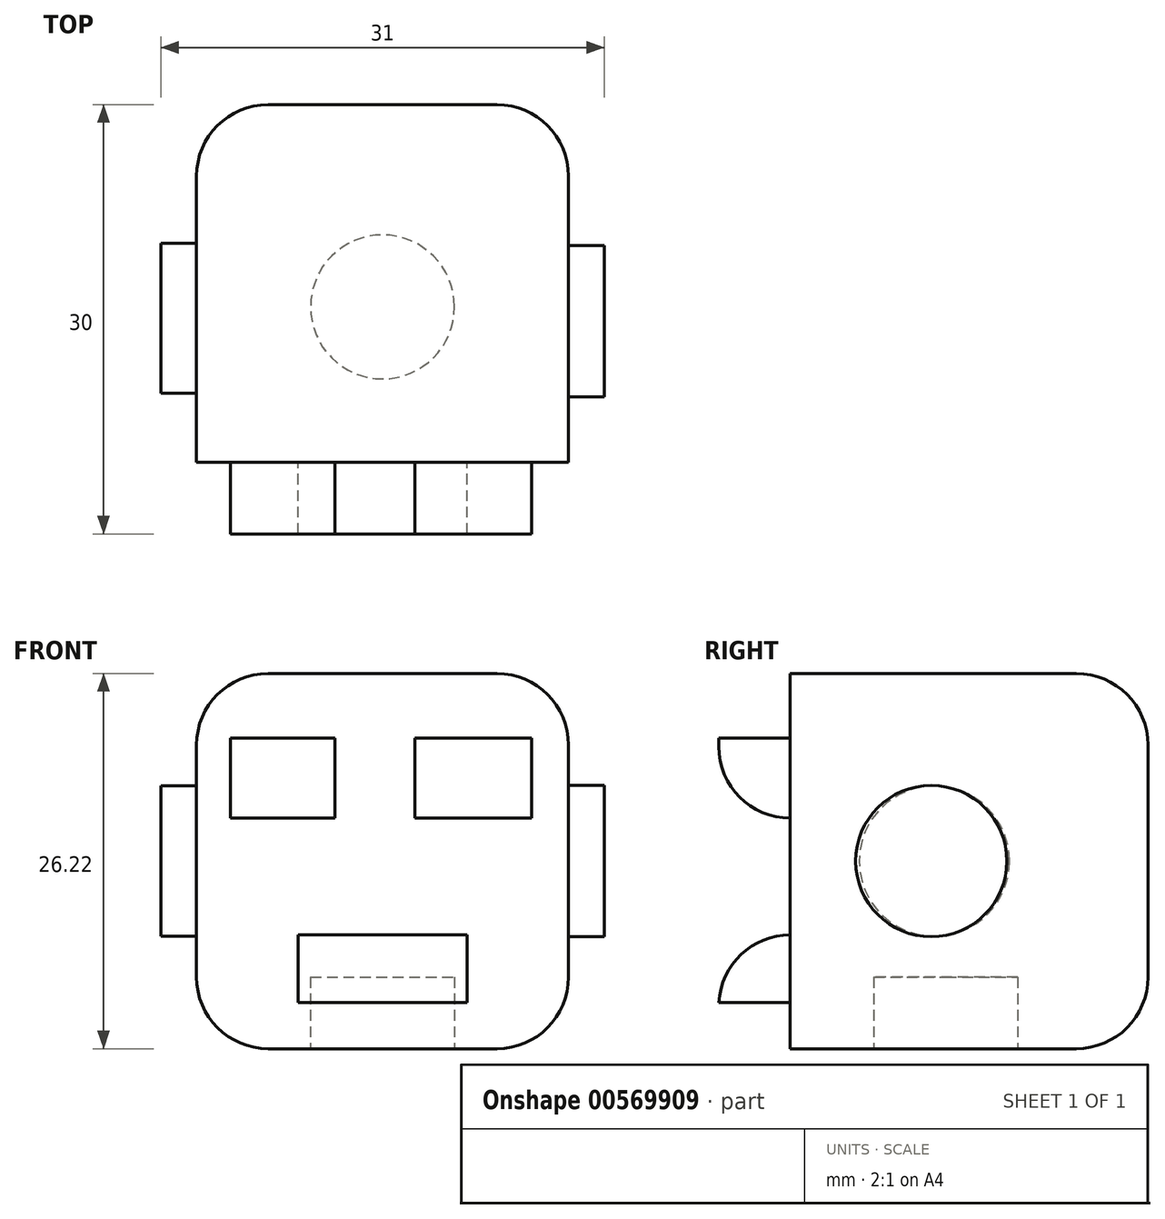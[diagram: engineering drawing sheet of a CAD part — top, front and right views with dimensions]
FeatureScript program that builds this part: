
annotation { "Feature Type Name" : "Feature", "Feature Type Description" : "" }
export const myFeature = defineFeature(function(context is Context, id is Id, definition is map)
    precondition{}
    {
        {
            var Q0;
            Q0=qCreatedBy(makeId("Front.planeOp"),FACE);
            var sketch = newSketch(context, id + "F0", { "sketchPlane" : qUnion([Q0])});
            skLineSegment(sketch, "E0.bottom", {"start": v(13, -13.1) * mm, "end": v(-13, -13.1) * mm});
            skLineSegment(sketch, "E0.top", {"start": v(13, 13.1) * mm, "end": v(-13, 13.1) * mm});
            skLineSegment(sketch, "E0.left", {"start": v(13, -13.1) * mm, "end": v(13, 13.1) * mm});
            skLineSegment(sketch, "E0.right", {"start": v(-13, -13.1) * mm, "end": v(-13, 13.1) * mm});
            skPoint(sketch, "E0.middle", {"position": v(0, 0) * mm});
            skSolve(sketch);
        }
        {
            var Q0;
            Q0=makeQuery(id+"F0.imprint","IMPRINT",FACE,{"disambiguationData":[TD([[makeQuery(id+"F0.imprint","IMPRINT",EDGE,{"derivedFrom":sQuery(id+"F0.wireOp",EDGE,"E0.bottom")}),-1.0]])]});
            extrude(context, id + "F1", {"entities" : qUnion([Q0]), "depth" : 25 * mm, "offsetDistance" : 25 * mm});
        }
        {
            var Q0;
            Q0=makeQuery(id+"F1.opExtrude","SWEPT_EDGE",EDGE,{"disambiguationData":[OSD([sQuery(id+"F0.wireOp",EDGE,"E0.top"),sQuery(id+"F0.wireOp",EDGE,"E0.right")])]});
            var Q1;
            Q1=makeQuery(id+"F1.opExtrude","CAP_EDGE",EDGE,{"disambiguationData":[OSD([sQuery(id+"F0.wireOp",EDGE,"E0.top")])],"isStart":true});
            var Q2;
            Q2=makeQuery(id+"F1.opExtrude","SWEPT_EDGE",EDGE,{"disambiguationData":[OSD([sQuery(id+"F0.wireOp",EDGE,"E0.top"),sQuery(id+"F0.wireOp",EDGE,"E0.left")])]});
            var Q3;
            Q3=makeQuery(id+"F1.opExtrude","CAP_EDGE",EDGE,{"disambiguationData":[OSD([sQuery(id+"F0.wireOp",EDGE,"E0.left")])],"isStart":true});
            var Q4;
            Q4=makeQuery(id+"F1.opExtrude","SWEPT_EDGE",EDGE,{"disambiguationData":[OSD([sQuery(id+"F0.wireOp",EDGE,"E0.bottom"),sQuery(id+"F0.wireOp",EDGE,"E0.left")])]});
            var Q5;
            Q5=makeQuery(id+"F1.opExtrude","SWEPT_EDGE",EDGE,{"disambiguationData":[OSD([sQuery(id+"F0.wireOp",EDGE,"E0.bottom"),sQuery(id+"F0.wireOp",EDGE,"E0.right")])]});
            var Q6;
            Q6=makeQuery(id+"F1.opExtrude","CAP_EDGE",EDGE,{"disambiguationData":[OSD([sQuery(id+"F0.wireOp",EDGE,"E0.bottom")])],"isStart":true});
            var Q7;
            Q7=makeQuery(id+"F1.opExtrude","CAP_EDGE",EDGE,{"disambiguationData":[OSD([sQuery(id+"F0.wireOp",EDGE,"E0.right")])],"isStart":true});
            fillet(context, id + "F2", {"entities" : qUnion([Q0, Q1, Q2, Q3, Q4, Q5, Q6, Q7]), "radius" : 5 * mm, "tangentPropagation" : true, "allowEdgeOverflow" : false});
        }
        {
            var Q0;
            Q0=makeQuery(id+"F1.opExtrude","CAP_FACE",FACE,{"disambiguationData":[OSD([sQuery(id+"F0.wireOp",EDGE,"E0.bottom"),sQuery(id+"F0.wireOp",EDGE,"E0.top"),sQuery(id+"F0.wireOp",EDGE,"E0.left"),sQuery(id+"F0.wireOp",EDGE,"E0.right")])],"isStart":false});
            var sketch = newSketch(context, id + "F3", { "sketchPlane" : qUnion([Q0])});
            skLineSegment(sketch, "E1.bottom", {"start": v(-3.33, 3) * mm, "end": v(-10.64, 3) * mm});
            skLineSegment(sketch, "E1.top", {"start": v(-3.33, 8.6) * mm, "end": v(-10.64, 8.6) * mm});
            skLineSegment(sketch, "E1.left", {"start": v(-3.33, 3) * mm, "end": v(-3.33, 8.6) * mm});
            skLineSegment(sketch, "E1.right", {"start": v(-10.64, 3) * mm, "end": v(-10.64, 8.6) * mm});
            skPoint(sketch, "E1.middle", {"position": v(-6.98, 5.8) * mm});
            skLineSegment(sketch, "E2.bottom", {"start": v(10.42, 3) * mm, "end": v(2.26, 3) * mm});
            skLineSegment(sketch, "E2.top", {"start": v(10.42, 8.6) * mm, "end": v(2.26, 8.6) * mm});
            skLineSegment(sketch, "E2.left", {"start": v(10.42, 3) * mm, "end": v(10.42, 8.6) * mm});
            skLineSegment(sketch, "E2.right", {"start": v(2.26, 3) * mm, "end": v(2.26, 8.6) * mm});
            skPoint(sketch, "E2.middle", {"position": v(6.34, 5.8) * mm});
            skSolve(sketch);
        }
        {
            var Q0;
            Q0=makeQuery(id+"F3.imprint","IMPRINT",FACE,{"disambiguationData":[TD([[makeQuery(id+"F3.imprint","IMPRINT",EDGE,{"derivedFrom":sQuery(id+"F3.wireOp",EDGE,"E1.bottom")}),1.0]])]});
            var sketch = newSketch(context, id + "F4", { "sketchPlane" : qUnion([Q0])});
            skLineSegment(sketch, "E3.bottom", {"start": v(5.9, -9.88) * mm, "end": v(-5.9, -9.88) * mm});
            skLineSegment(sketch, "E3.top", {"start": v(5.9, -5.16) * mm, "end": v(-5.9, -5.16) * mm});
            skLineSegment(sketch, "E3.left", {"start": v(5.9, -9.88) * mm, "end": v(5.9, -5.16) * mm});
            skLineSegment(sketch, "E3.right", {"start": v(-5.9, -9.88) * mm, "end": v(-5.9, -5.16) * mm});
            skPoint(sketch, "E3.middle", {"position": v(0, -7.52) * mm});
            skSolve(sketch);
        }
        {
            var Q0;
            Q0=makeQuery(id+"F3.imprint","IMPRINT",FACE,{"disambiguationData":[TD([[makeQuery(id+"F3.imprint","IMPRINT",EDGE,{"derivedFrom":sQuery(id+"F3.wireOp",EDGE,"E2.bottom")}),-1.0]])]});
            var Q1;
            Q1=makeQuery(id+"F3.imprint","IMPRINT",FACE,{"disambiguationData":[TD([[makeQuery(id+"F3.imprint","IMPRINT",EDGE,{"derivedFrom":sQuery(id+"F3.wireOp",EDGE,"E1.bottom")}),-1.0]])]});
            var Q2;
            Q2=makeQuery(id+"F4.imprint","IMPRINT",FACE,{"disambiguationData":[TD([[makeQuery(id+"F4.imprint","IMPRINT",EDGE,{"derivedFrom":sQuery(id+"F4.wireOp",EDGE,"E3.bottom")}),-1.0]])]});
            extrude(context, id + "F5", {"entities" : qUnion([Q0, Q1, Q2]), "operationType" : NewBodyOperationType.ADD, "depth" : 5 * mm, "offsetDistance" : 25 * mm});
        }
        {
            var Q0;
            Q0=makeQuery(id+"F5.opExtrude","CAP_EDGE",EDGE,{"disambiguationData":[OSD([sQuery(id+"F3.wireOp",EDGE,"E1.bottom")])],"isStart":false});
            var Q1;
            Q1=makeQuery(id+"F5.opExtrude","CAP_EDGE",EDGE,{"disambiguationData":[OSD([sQuery(id+"F3.wireOp",EDGE,"E2.bottom")])],"isStart":false});
            var Q2;
            Q2=makeQuery(id+"F5.opExtrude","CAP_EDGE",EDGE,{"disambiguationData":[OSD([sQuery(id+"F4.wireOp",EDGE,"E3.top")])],"isStart":false});
            fillet(context, id + "F6", {"entities" : qUnion([Q0, Q1, Q2]), "radius" : 5 * mm, "tangentPropagation" : true, "allowEdgeOverflow" : false});
        }
        {
            var Q0;
            Q0=makeQuery(id+"F1.opExtrude","SWEPT_FACE",FACE,{"disambiguationData":[OSD([sQuery(id+"F0.wireOp",EDGE,"E0.left")])]});
            var sketch = newSketch(context, id + "F7", { "sketchPlane" : qUnion([Q0])});
            skCircle(sketch, "E4", {"center": v(-15.15, 0) * mm, "radius": 5.29 * mm});
            skSolve(sketch);
        }
        {
            var Q0;
            Q0=makeQuery(id+"F1.opExtrude","SWEPT_FACE",FACE,{"disambiguationData":[OSD([sQuery(id+"F0.wireOp",EDGE,"E0.right")])]});
            var sketch = newSketch(context, id + "F8", { "sketchPlane" : qUnion([Q0])});
            skCircle(sketch, "E5", {"center": v(14.93, 0) * mm, "radius": 5.25 * mm});
            skSolve(sketch);
        }
        {
            var Q0;
            Q0=makeQuery(id+"F7.imprint","IMPRINT",FACE,{"disambiguationData":[TD([[makeQuery(id+"F7.imprint","IMPRINT",EDGE,{"derivedFrom":sQuery(id+"F7.wireOp",EDGE,"E4")}),1.0]])]});
            extrude(context, id + "F9", {"entities" : qUnion([Q0]), "operationType" : NewBodyOperationType.ADD, "depth" : 2.5 * mm, "offsetDistance" : 25 * mm});
        }
        {
            var Q0;
            Q0=makeQuery(id+"F8.imprint","IMPRINT",FACE,{"disambiguationData":[TD([[makeQuery(id+"F8.imprint","IMPRINT",EDGE,{"derivedFrom":sQuery(id+"F8.wireOp",EDGE,"E5")}),1.0]])]});
            extrude(context, id + "F10", {"entities" : qUnion([Q0]), "operationType" : NewBodyOperationType.ADD, "depth" : 2.5 * mm, "offsetDistance" : 25 * mm});
        }
        {
            var Q0;
            Q0=makeQuery(id+"F1.opExtrude","SWEPT_FACE",FACE,{"disambiguationData":[OSD([sQuery(id+"F0.wireOp",EDGE,"E0.bottom")])]});
            var sketch = newSketch(context, id + "F11", { "sketchPlane" : qUnion([Q0])});
            skCircle(sketch, "E6", {"center": v(0, 14.13) * mm, "radius": 5.03 * mm});
            skSolve(sketch);
        }
        {
            var Q0;
            Q0=makeQuery(id+"F11.imprint","IMPRINT",FACE,{"disambiguationData":[TD([[makeQuery(id+"F11.imprint","IMPRINT",EDGE,{"derivedFrom":sQuery(id+"F11.wireOp",EDGE,"E6")}),1.0]])]});
            extrude(context, id + "F12", {"entities" : qUnion([Q0]), "operationType" : NewBodyOperationType.REMOVE, "oppositeDirection" : true, "depth" : 5 * mm, "offsetDistance" : 25 * mm});
        }
    });
